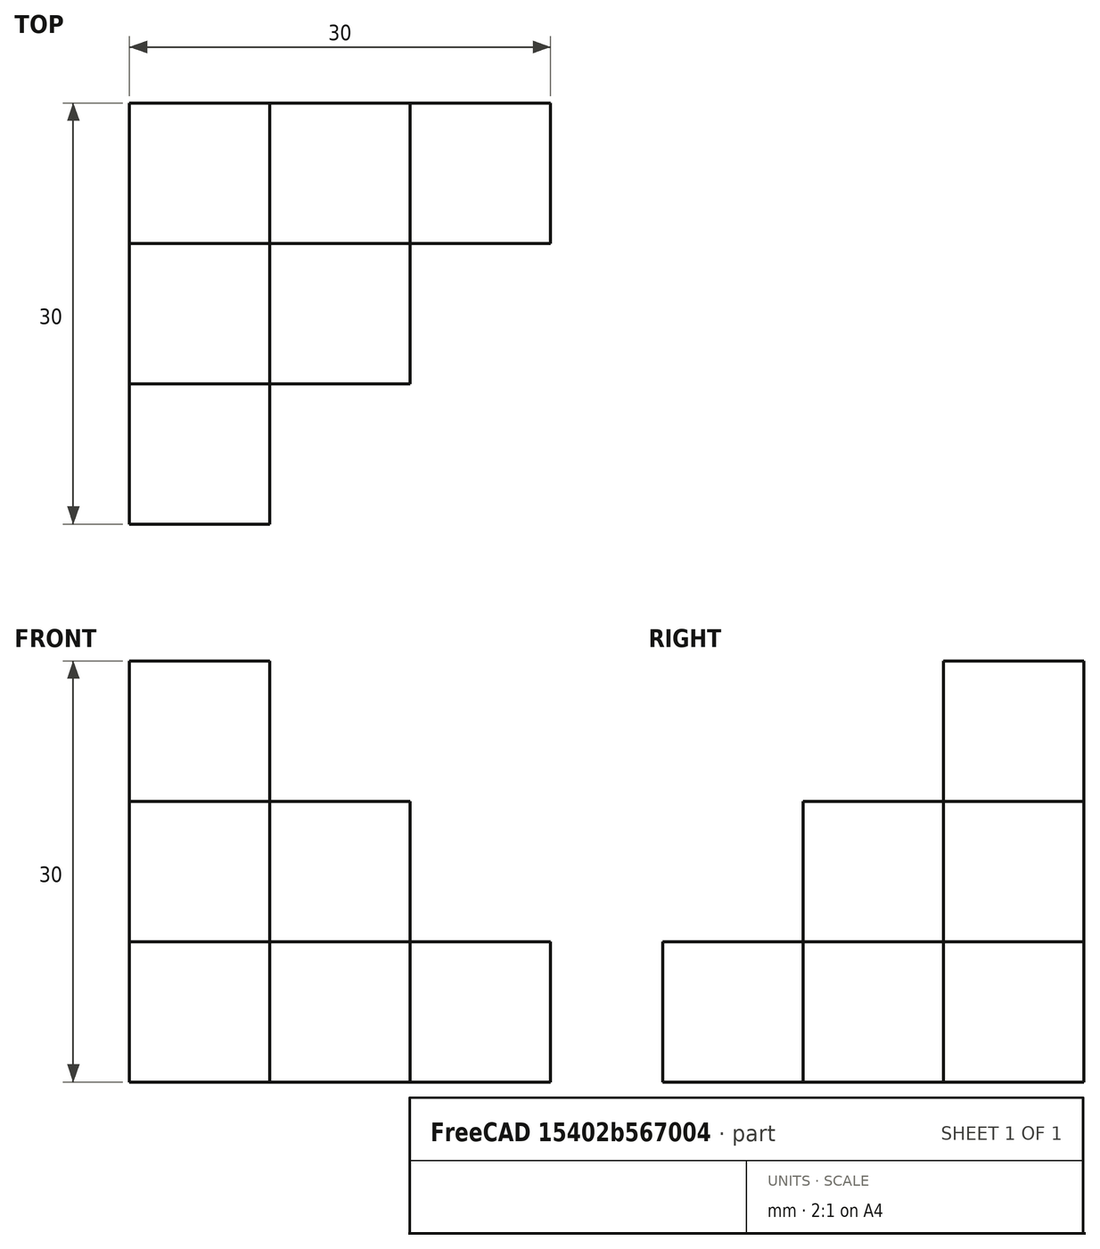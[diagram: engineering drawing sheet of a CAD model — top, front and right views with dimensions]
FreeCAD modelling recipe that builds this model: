
FCSTD DOCUMENT  (FreeCAD 1.0R39285 (Git))
Label: ojt1_t04r01_qbert 3 levels
License: All rights reserved
objects: Part::Box×6
note: 6 computed .brp shape members not serialized (recipe doc carries the construction recipe); baked Part::Feature solids carry a one-line shape summary decoded from their .brp

FEATURE [Part::Box] Box  label="Cub"
  AttacherType = Attacher::AttachEngine3D
  Height = 30
  Length = 10
  Width = 10
FEATURE [Part::Box] Box001  label="Cub001"
  AttacherType = Attacher::AttachEngine3D
  Height = 20
  Length = 10
  Placement = pos=(10,0,0) rot=(0,0,1;0rad)
  Width = 10
FEATURE [Part::Box] Box002  label="Cub002"
  AttacherType = Attacher::AttachEngine3D
  Height = 20
  Length = 10
  Placement = pos=(0,-10,0) rot=(0,0,1;0rad)
  Width = 10
FEATURE [Part::Box] Box003  label="Cub003"
  AttacherType = Attacher::AttachEngine3D
  Height = 10
  Length = 10
  Placement = pos=(10,-10,0) rot=(0,0,1;0rad)
  Width = 10
FEATURE [Part::Box] Box004  label="Cub004"
  AttacherType = Attacher::AttachEngine3D
  Height = 10
  Length = 10
  Placement = pos=(0,-20,0) rot=(0,0,1;0rad)
  Width = 10
FEATURE [Part::Box] Box005  label="Cub005"
  AttacherType = Attacher::AttachEngine3D
  Height = 10
  Length = 10
  Placement = pos=(20,0,0) rot=(0,0,1;0rad)
  Width = 10
